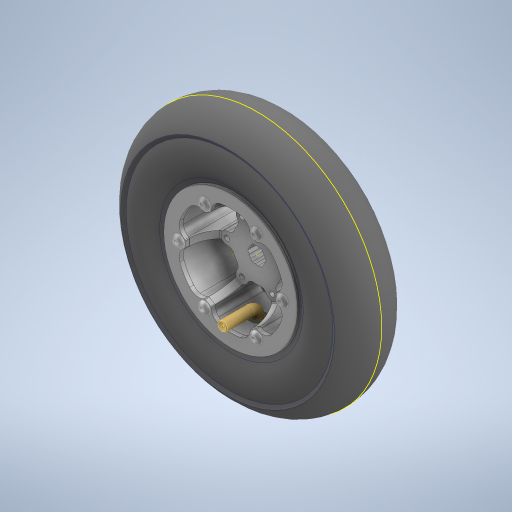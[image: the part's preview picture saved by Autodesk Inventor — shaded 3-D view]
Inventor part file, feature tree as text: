
AUTODESK INVENTOR PART (.ipt)
format: ipt  version: 2023 (Build 270158000, 158)  size: 5,485,568 bytes
history: native  units: in
note: dims shown in document units (in); Inventor stores cm internally (conversion verified against a paired STEP export)
features: other x17, sketch x1
ambient origin geometry x8: Origin, YZ Plane, XZ Plane, XY Plane, X Axis, Y Axis, Z Axis, Center Point
bodies: Solid1 (feature_tree), Solid2 (feature_tree), Solid3 (feature_tree), Solid4 (feature_tree), Solid5 (feature_tree), Solid6 (feature_tree), Solid7 (feature_tree), Solid8 (feature_tree), Solid9 (feature_tree), Solid10 (feature_tree), Solid11 (feature_tree), Solid12 (feature_tree), Solid13 (feature_tree), Solid14 (feature_tree), Solid15 (feature_tree), Solid16 (feature_tree), Solid17 (feature_tree)
feature tree (18):
  sketch  "Sketch1"
  other  "Aluminum 8IN Pneumatic Wheel 500IN Hex BoreCore_1:1"
  other  "Aluminum 8IN Pneumatic Wheel Rim_2:1"
  other  "Aluminum 8IN Pneumatic Wheel Rim_3:1"
  other  "Valve_4:1"
  other  "Tire_5:1"
  other  "BHCS 10-32 x 0.500_91255A265_6:1"
  other  "BHCS 10-32 x 0.500_91255A265_7:1"
  other  "BHCS 10-32 x 0.500_91255A265_8:1"
  other  "BHCS 10-32 x 0.500_91255A265_9:1"
  other  "BHCS 10-32 x 0.500_91255A265_10:1"
  other  "BHCS 10-32 x 0.500_91255A265_11:1"
  other  "BHCS 10-32 x 0.500_91255A265_12:1"
  other  "BHCS 10-32 x 0.500_91255A265_13:1"
  other  "BHCS 10-32 x 0.500_91255A265_14:1"
  other  "BHCS 10-32 x 0.500_91255A265_15:1"
  other  "BHCS 10-32 x 0.500_91255A265_16:1"
  other  "BHCS 10-32 x 0.500_91255A265_17:1"
